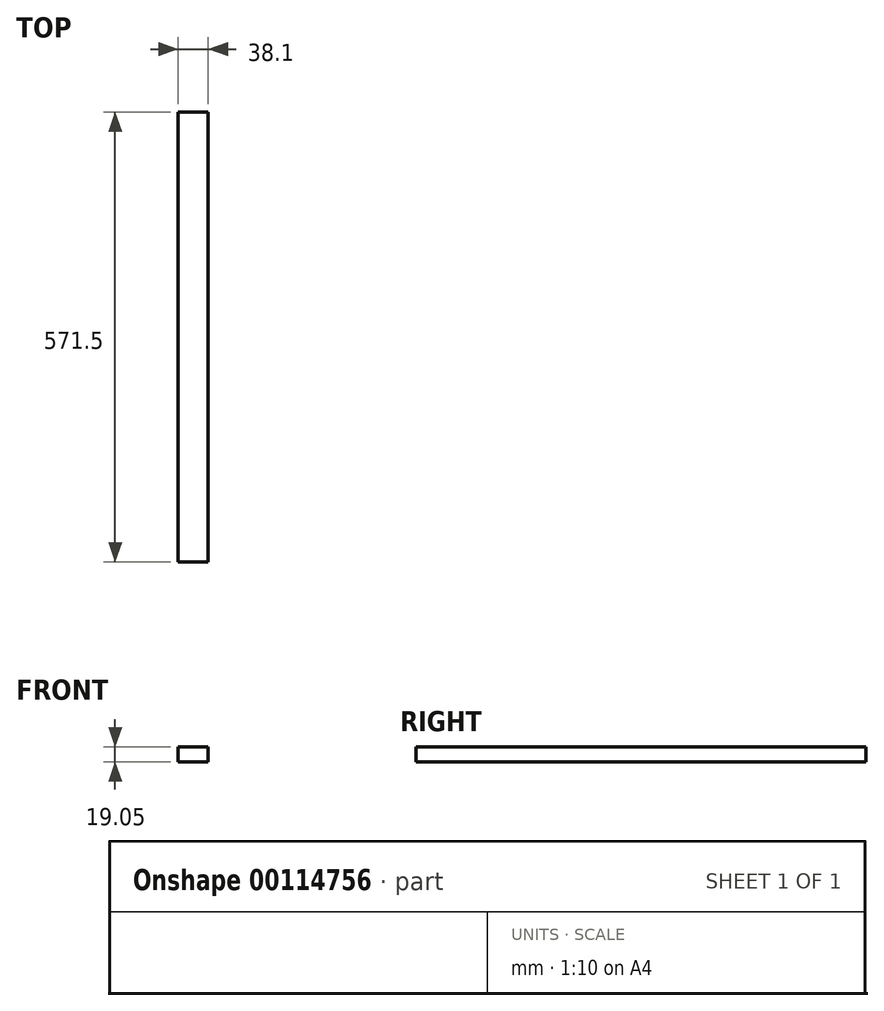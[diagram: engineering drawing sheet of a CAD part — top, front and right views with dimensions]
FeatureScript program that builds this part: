
annotation { "Feature Type Name" : "Feature", "Feature Type Description" : "" }
export const myFeature = defineFeature(function(context is Context, id is Id, definition is map)
    precondition{}
    {
        {
            var Q0;
            Q0=qCreatedBy(makeId("Top.planeOp"),FACE);
            var sketch = newSketch(context, id + "F0", { "sketchPlane" : qUnion([Q0])});
            skLineSegment(sketch, "E0.bottom", {"start": v(0, 0) * mm, "end": v(38.1, 0) * mm});
            skLineSegment(sketch, "E0.top", {"start": v(0, 571.5) * mm, "end": v(38.1, 571.5) * mm});
            skLineSegment(sketch, "E0.left", {"start": v(0, 0) * mm, "end": v(0, 571.5) * mm});
            skLineSegment(sketch, "E0.right", {"start": v(38.1, 0) * mm, "end": v(38.1, 571.5) * mm});
            skSolve(sketch);
        }
        {
            var Q0;
            Q0=qSketchRegion(id+"F0",true);
            extrude(context, id + "F1", {"entities" : qUnion([Q0]), "depth" : 19.05 * mm});
        }
    });
